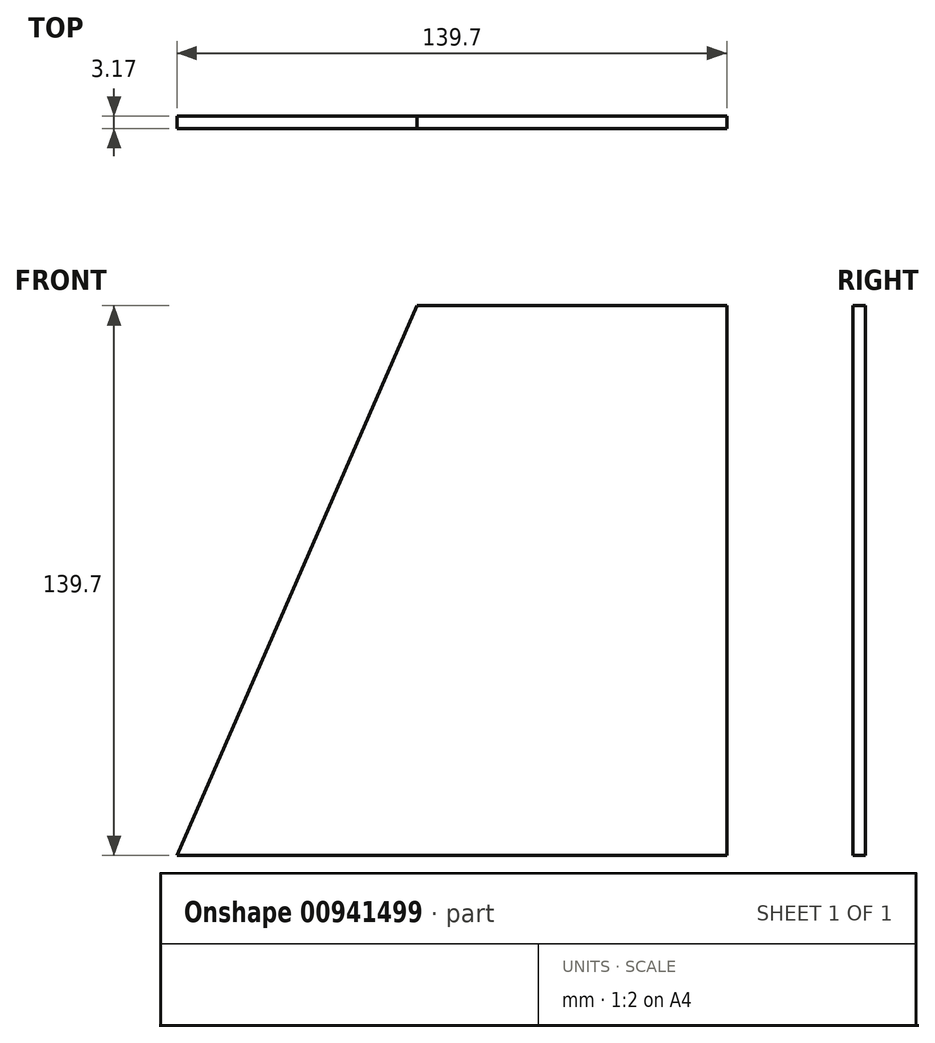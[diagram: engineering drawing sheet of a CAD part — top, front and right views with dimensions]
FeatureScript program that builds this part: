
annotation { "Feature Type Name" : "Feature", "Feature Type Description" : "" }
export const myFeature = defineFeature(function(context is Context, id is Id, definition is map)
    precondition{}
    {
        {
            var Q0;
            Q0=qCreatedBy(makeId("Front.planeOp"),FACE);
            var sketch = newSketch(context, id + "F0", { "sketchPlane" : qUnion([Q0])});
            skLineSegment(sketch, "E0", {"start": v(74.82, -76.51) * mm, "end": v(74.82, 63.19) * mm});
            skLineSegment(sketch, "E1", {"start": v(74.82, 63.19) * mm, "end": v(-3.92, 63.19) * mm});
            skLineSegment(sketch, "E2", {"start": v(-3.92, 63.19) * mm, "end": v(-64.88, -76.51) * mm});
            skLineSegment(sketch, "E3", {"start": v(-64.88, -76.51) * mm, "end": v(74.82, -76.51) * mm});
            skSolve(sketch);
        }
        {
            var Q0;
            Q0 = qSketchRegion(id + "F0", true);
            extrude(context, id + "F1", {"entities" : qUnion([Q0]), "depth" : 3.17 * mm, "offsetDistance" : 25.4 * mm});
        }
    });
